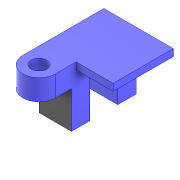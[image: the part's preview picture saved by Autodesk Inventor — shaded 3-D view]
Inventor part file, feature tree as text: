
AUTODESK INVENTOR PART (.ipt)
format: ipt  version: 2022 (Build 260153000, 153)  size: 145,408 bytes
history: native  units: mm
features: sketch x4, extrude x3, hole x1, projected_geometry x1
ambient origin geometry x8: Origin, YZ Plane, XZ Plane, XY Plane, X Axis, Y Axis, Z Axis, Center Point
bodies: Solid1 (feature_tree)
feature tree (9):
  extrude  "Extrusion1"  Depth=15.0mm
  extrude  "Extrusion2"  Depth=8.0mm
  extrude  "Extrusion3"  Depth=1.5mm TaperAngle=0.0deg
  hole  "Hole1"  [1 undecoded]
  sketch  "Sketch1"  dims[d0=13.0mm d1=15.0mm]
  sketch  "Sketch2"  dims[d3=7.0mm d4=8.0mm]
  projected_geometry  "Projected Loop1"
  sketch  "Sketch3"  dims[d5=8.0mm d6=1.5mm d7=0.0mm]
  sketch  "Sketch4"  dims[d8=3.0mm d9=0.0mm d10=4.0mm d11=8.0mm d12=1.0mm d13=4.0mm d14=3.0mm d15=0.0mm d16=3.4mm d17=6.0mm d18=4.0mm d19=2.0mm d20=90.0deg d21=8.0mm d22=20.594885mm]
note: 1 required parameter value undecoded (feature->parameter linkage not recoverable at this tier; creation-order binding heuristic only, values carry confidence <= 0.55)
